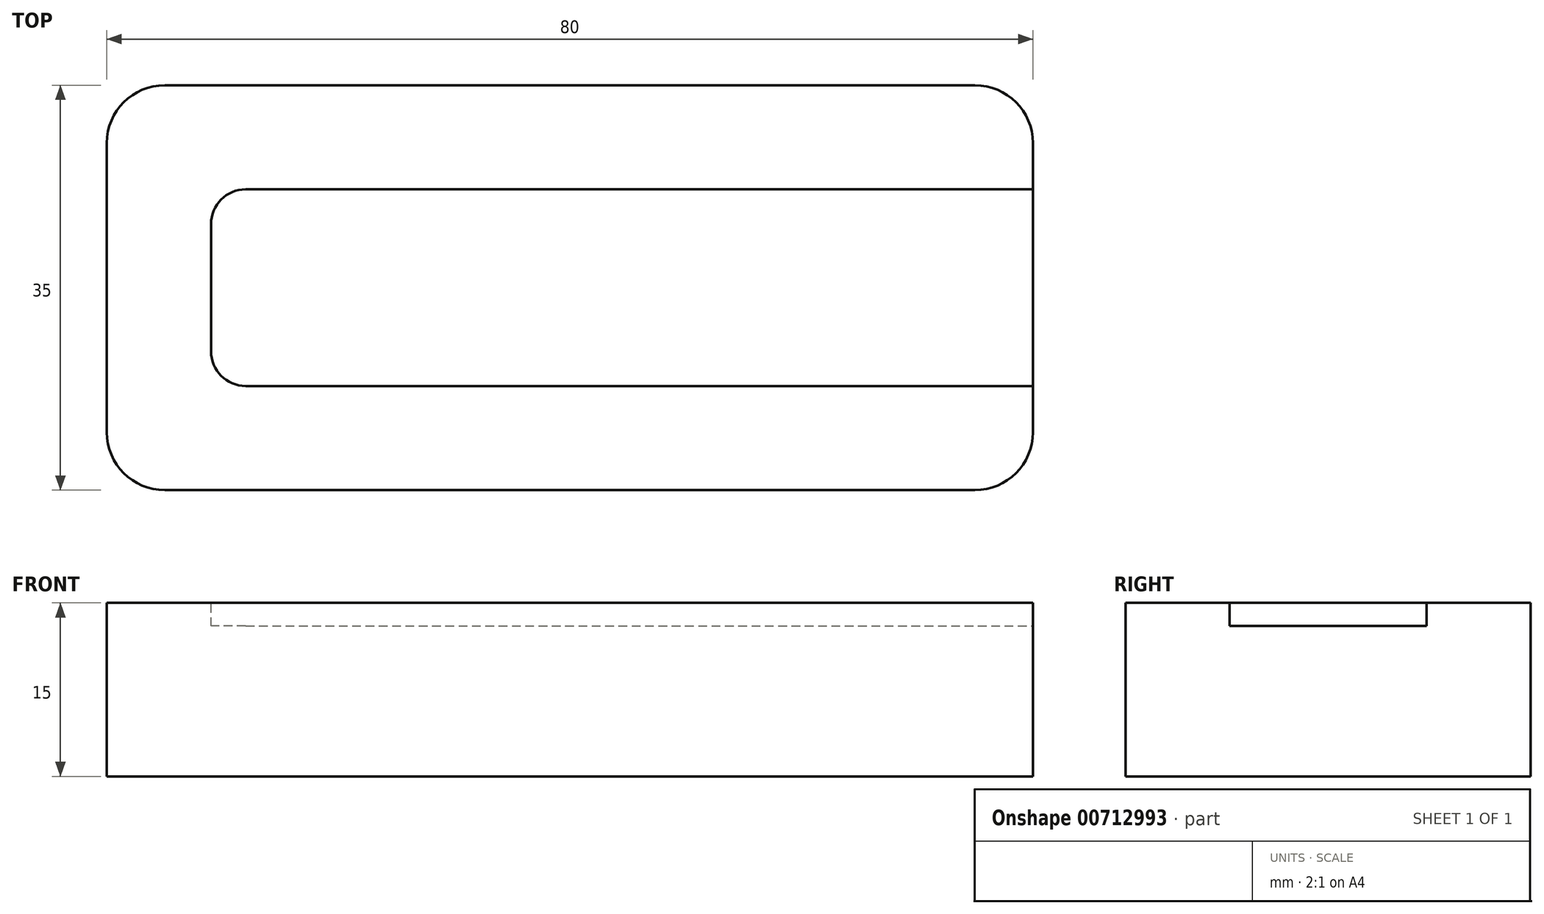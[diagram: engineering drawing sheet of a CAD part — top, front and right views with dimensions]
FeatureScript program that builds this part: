
annotation { "Feature Type Name" : "Feature", "Feature Type Description" : "" }
export const myFeature = defineFeature(function(context is Context, id is Id, definition is map)
    precondition{}
    {
        {
            var Q0;
            Q0=qCreatedBy(makeId("Top.planeOp"),FACE);
            var sketch = newSketch(context, id + "F0", { "sketchPlane" : qUnion([Q0])});
            skLineSegment(sketch, "E0.bottom", {"start": v(0, 0) * mm, "end": v(80, 0) * mm});
            skLineSegment(sketch, "E0.top", {"start": v(0, 35) * mm, "end": v(80, 35) * mm});
            skLineSegment(sketch, "E0.left", {"start": v(0, 0) * mm, "end": v(0, 35) * mm});
            skLineSegment(sketch, "E0.right", {"start": v(80, 0) * mm, "end": v(80, 35) * mm});
            skSolve(sketch);
        }
        {
            var Q0;
            Q0 = qSketchRegion(id + "F0", true);
            extrude(context, id + "F1", {"entities" : qUnion([Q0]), "depth" : 15 * mm, "offsetDistance" : 25 * mm});
        }
        {
            var Q0;
            Q0=makeQuery(id+"F1.opExtrude","SWEPT_EDGE",EDGE,{"disambiguationData":[OSD([sQuery(id+"F0.wireOp",EDGE,"E0.bottom"),sQuery(id+"F0.wireOp",EDGE,"E0.left")])]});
            var Q1;
            Q1=makeQuery(id+"F1.opExtrude","SWEPT_EDGE",EDGE,{"disambiguationData":[OSD([sQuery(id+"F0.wireOp",EDGE,"E0.bottom"),sQuery(id+"F0.wireOp",EDGE,"E0.right")])]});
            var Q2;
            Q2=makeQuery(id+"F1.opExtrude","SWEPT_EDGE",EDGE,{"disambiguationData":[OSD([sQuery(id+"F0.wireOp",EDGE,"E0.top"),sQuery(id+"F0.wireOp",EDGE,"E0.right")])]});
            var Q3;
            Q3=makeQuery(id+"F1.opExtrude","SWEPT_EDGE",EDGE,{"disambiguationData":[OSD([sQuery(id+"F0.wireOp",EDGE,"E0.top"),sQuery(id+"F0.wireOp",EDGE,"E0.left")])]});
            fillet(context, id + "F2", {"entities" : qUnion([Q0, Q1, Q2, Q3]), "radius" : 5 * mm, "tangentPropagation" : true, "allowEdgeOverflow" : false});
        }
        {
            var Q0;
            Q0=makeQuery(id+"F1.opExtrude","CAP_FACE",FACE,{"disambiguationData":[OSD([sQuery(id+"F0.wireOp",EDGE,"E0.bottom"),sQuery(id+"F0.wireOp",EDGE,"E0.top"),sQuery(id+"F0.wireOp",EDGE,"E0.left"),sQuery(id+"F0.wireOp",EDGE,"E0.right")])],"isStart":false});
            var sketch = newSketch(context, id + "F3", { "sketchPlane" : qUnion([Q0])});
            skLineSegment(sketch, "E1.bottom", {"start": v(12, 26) * mm, "end": v(86.1, 26) * mm});
            skLineSegment(sketch, "E1.top", {"start": v(12, 9) * mm, "end": v(86.1, 9) * mm});
            skLineSegment(sketch, "E1.left", {"start": v(9, 23) * mm, "end": v(9, 12) * mm});
            skLineSegment(sketch, "E1.right", {"start": v(86.1, 26) * mm, "end": v(86.1, 9) * mm});
            skPoint(sketch, "E2.visualSharp", {"position": v(9, 26) * mm});
            skArc(sketch, "E2.filletArc", {"start": v(12, 26) * mm, "mid": v(9.88, 25.12) * mm, "end": v(9, 23) * mm});
            skPoint(sketch, "E3.visualSharp", {"position": v(9, 9) * mm});
            skArc(sketch, "E3.filletArc", {"start": v(9, 12) * mm, "mid": v(9.88, 9.88) * mm, "end": v(12, 9) * mm});
            skSolve(sketch);
        }
        {
            var Q0;
            Q0=makeQuery(id+"F3.imprint","IMPRINT",FACE,{"disambiguationData":[TD([[makeQuery(id+"F3.imprint","IMPRINT",EDGE,{"derivedFrom":sQuery(id+"F3.wireOp",EDGE,"E1.left")}),1.0]])]});
            extrude(context, id + "F4", {"entities" : qUnion([Q0]), "operationType" : NewBodyOperationType.REMOVE, "oppositeDirection" : true, "depth" : 2 * mm, "offsetDistance" : 25 * mm});
        }
    });
